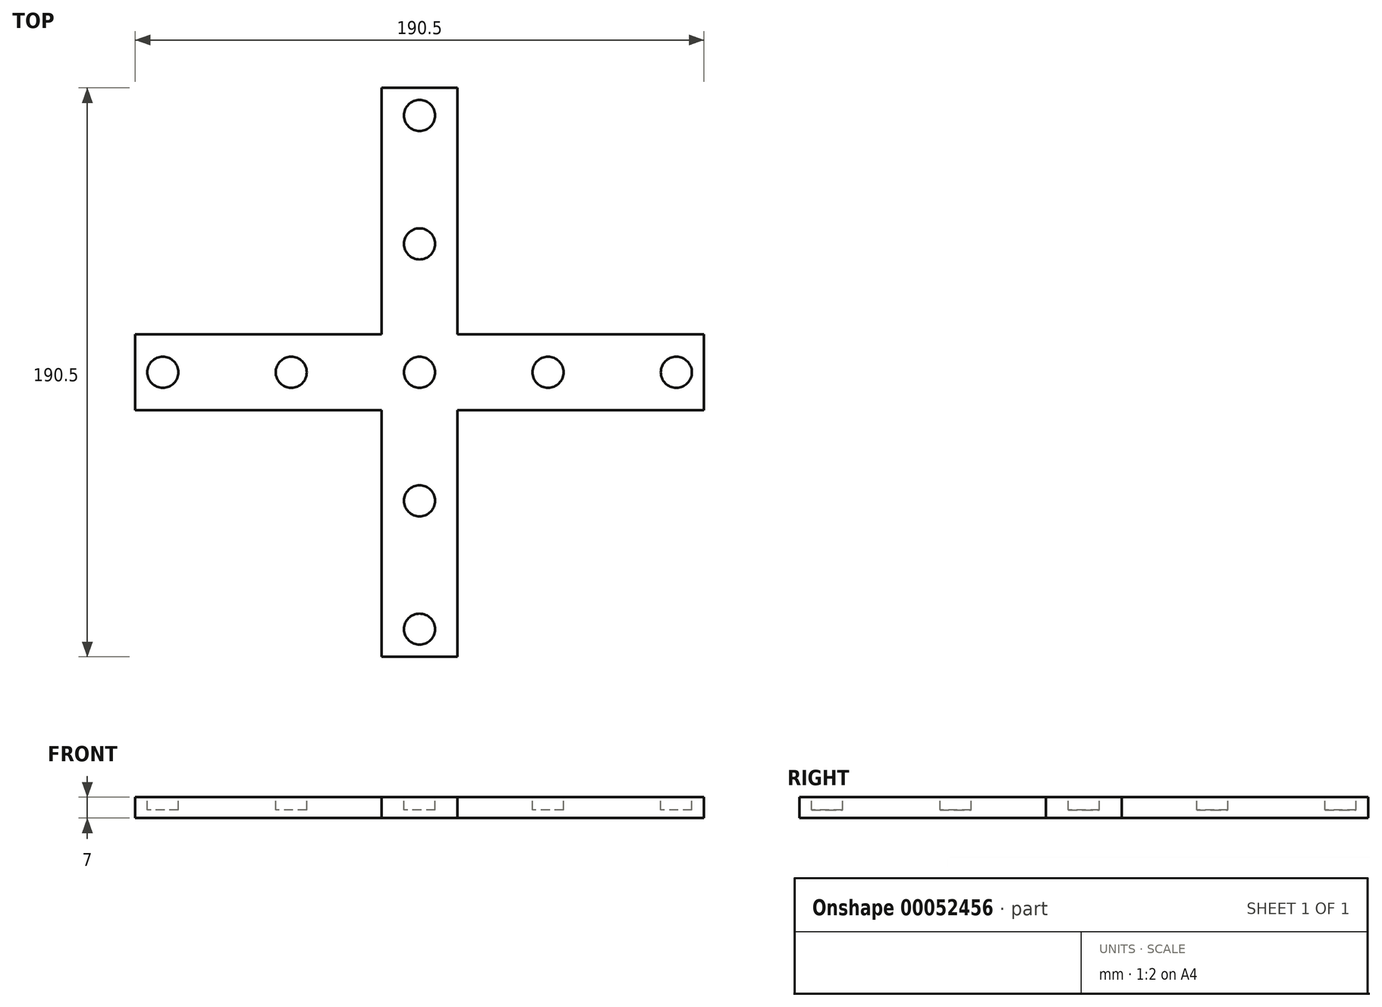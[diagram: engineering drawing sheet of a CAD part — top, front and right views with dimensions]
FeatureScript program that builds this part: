
annotation { "Feature Type Name" : "Feature", "Feature Type Description" : "" }
export const myFeature = defineFeature(function(context is Context, id is Id, definition is map)
    precondition{}
    {
        {
            var Q0;
            Q0=qCreatedBy(makeId("Top.planeOp"),FACE);
            var sketch = newSketch(context, id + "F0", { "sketchPlane" : qUnion([Q0])});
            skLineSegment(sketch, "E0.rect.bottom", {"start": v(-95.25, -12.7) * mm, "end": v(-12.7, -12.7) * mm});
            skLineSegment(sketch, "E0.rect.top", {"start": v(-95.25, 12.7) * mm, "end": v(-12.7, 12.7) * mm});
            skLineSegment(sketch, "E0.rect.left", {"start": v(-95.25, -12.7) * mm, "end": v(-95.25, 12.7) * mm});
            skLineSegment(sketch, "E0.rect.right", {"start": v(95.25, -12.7) * mm, "end": v(95.25, 12.7) * mm});
            skPoint(sketch, "E0.rect.middle", {"position": v(0, 0) * mm});
            skLineSegment(sketch, "E1.rect.bottom", {"start": v(12.7, 95.25) * mm, "end": v(-12.7, 95.25) * mm});
            skLineSegment(sketch, "E1.rect.top", {"start": v(12.7, -95.25) * mm, "end": v(-12.7, -95.25) * mm});
            skLineSegment(sketch, "E1.rect.left", {"start": v(12.7, 95.25) * mm, "end": v(12.7, 12.7) * mm});
            skLineSegment(sketch, "E1.rect.right", {"start": v(-12.7, 95.25) * mm, "end": v(-12.7, 12.7) * mm});
            skLineSegment(sketch, "E2.trimOffspring", {"start": v(-12.7, -12.7) * mm, "end": v(-12.7, -95.25) * mm});
            skLineSegment(sketch, "E3.trimOffspring", {"start": v(12.7, 12.7) * mm, "end": v(95.25, 12.7) * mm});
            skLineSegment(sketch, "E4.trimOffspring", {"start": v(12.7, -12.7) * mm, "end": v(12.7, -95.25) * mm});
            skLineSegment(sketch, "E5.trimOffspring", {"start": v(12.7, -12.7) * mm, "end": v(95.25, -12.7) * mm});
            skSolve(sketch);
        }
        {
            var Q0;
            Q0 = qSketchRegion(id + "F0", true);
            extrude(context, id + "F1", {"entities" : qUnion([Q0]), "depth" : 7 * mm});
        }
        {
            var Q0;
            Q0=makeQuery(id+"F1.opExtrude","CAP_FACE",FACE,{"disambiguationData":[OSD([sQuery(id+"F0.wireOp",EDGE,"E0.rect.bottom"),sQuery(id+"F0.wireOp",EDGE,"E0.rect.top"),sQuery(id+"F0.wireOp",EDGE,"E0.rect.left"),sQuery(id+"F0.wireOp",EDGE,"E0.rect.right"),sQuery(id+"F0.wireOp",EDGE,"E1.rect.bottom"),sQuery(id+"F0.wireOp",EDGE,"E1.rect.top"),sQuery(id+"F0.wireOp",EDGE,"E1.rect.left"),sQuery(id+"F0.wireOp",EDGE,"E1.rect.right")])],"isStart":false});
            var sketch = newSketch(context, id + "F2", { "sketchPlane" : qUnion([Q0])});
            skCircle(sketch, "E6", {"center": v(0, 0) * mm, "radius": 5.2 * mm});
            skPoint(sketch, "E7.orphan", {"position": v(-95.25, 0) * mm});
            skCircle(sketch, "E8", {"center": v(-43, 0) * mm, "radius": 5.2 * mm});
            skCircle(sketch, "E9", {"center": v(-86, 0) * mm, "radius": 5.2 * mm});
            skCircle(sketch, "E10.MirrorC", {"center": v(86, 0) * mm, "radius": 5.2 * mm});
            skCircle(sketch, "E11.MirrorC", {"center": v(43, 0) * mm, "radius": 5.2 * mm});
            skCircle(sketch, "E12.1.0", {"center": v(0, -86) * mm, "radius": 5.2 * mm});
            skCircle(sketch, "E12.1.1", {"center": v(0, -43) * mm, "radius": 5.2 * mm});
            skCircle(sketch, "E12.1.2", {"center": v(0, 43) * mm, "radius": 5.2 * mm});
            skCircle(sketch, "E12.1.3", {"center": v(0, 86) * mm, "radius": 5.2 * mm});
            skSolve(sketch);
        }
        {
            var Q0;
            Q0 = qSketchRegion(id + "F2", true);
            extrude(context, id + "F3", {"entities" : qUnion([Q0]), "operationType" : NewBodyOperationType.REMOVE, "oppositeDirection" : true, "depth" : 4.3 * mm});
        }
    });
